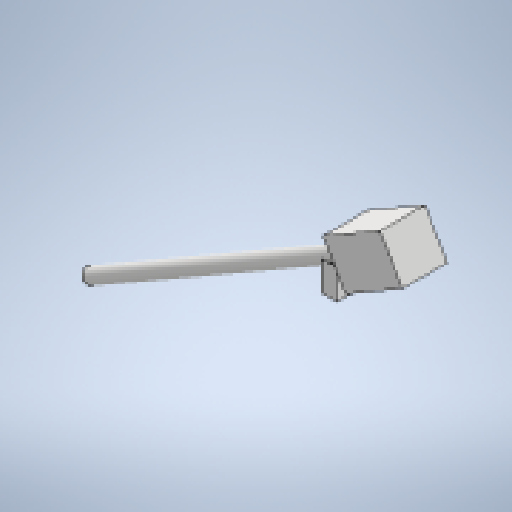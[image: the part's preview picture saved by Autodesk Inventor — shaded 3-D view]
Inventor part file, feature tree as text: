
AUTODESK INVENTOR PART (.ipt)
format: ipt  version: 2025.1 (Build 291241020, 241B)  size: 177,664 bytes
history: native  units: mm
features: sketch x2, extrude x2, plane x1, sweep x1
ambient origin geometry x8: Origin, YZ Plane, XZ Plane, XY Plane, X Axis, Y Axis, Z Axis, Center Point
bodies: Body1 (feature_tree)
feature tree (6):
  sketch  "Sketch2"  dims[d3=30.0deg d4=2000.0mm]
  plane  "Work Plane1"
  sweep  "Sweep1"
  extrude  "Extrusion2"  Depth=300.0mm
  extrude  "Extrusion3"  TaperAngle=0.0deg  [1 undecoded]
  sketch  "Sketch3"  dims[d6=100.0mm d7=3.0mm d8=0.0mm d9=0.0mm d10=2250.0mm d11=500.0mm d12=500.0mm d13=300.0mm d14=150.0mm d15=60.0mm d16=100.0mm d17=200.0mm d18=150.0mm d19=100.0mm d20=0.0mm d21=300.0mm d22=0.0mm]
note: 1 required parameter value undecoded (feature->parameter linkage not recoverable at this tier; creation-order binding heuristic only, values carry confidence <= 0.55)
